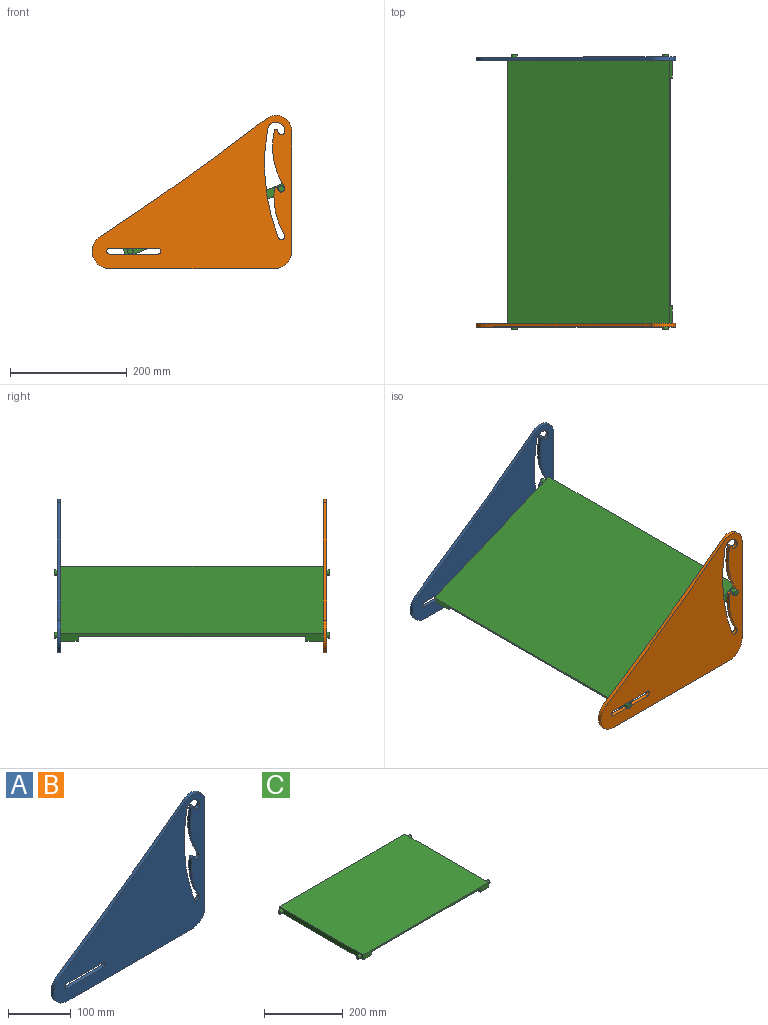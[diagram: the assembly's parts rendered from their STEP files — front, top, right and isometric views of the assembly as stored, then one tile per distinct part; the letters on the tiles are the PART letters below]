
ASSEMBLY  parts=3 mates=1
PART A: 21 faces, bbox 341.7x6x262.6 mm
  f0: cylinder r=5mm len=10mm, axis (0,1,0), area 94.2mm2, adj f1,f18,f19,f20
  f1: plane 82.5x6mm, normal (0,0,1), area 495mm2, adj f0,f2,f19,f20
  f2: cylinder r=5mm len=10mm, axis (0,1,0), area 94.2mm2, adj f1,f18,f19,f20
  f3: plane 281.72x6mm, normal (0,0,-1), area 1690.3mm2, adj f4,f16,f19,f20
  f4: cylinder r=30mm len=30mm, axis (0,1,0), area 282.7mm2, adj f3,f5,f19,f20
  f5: plane 205.78x6mm, normal (1,0,0), area 1234.7mm2, adj f4,f6,f19,f20
  f6: cylinder r=26.85mm len=42.37mm, axis (0,1,0), area 352.3mm2, adj f5,f7,f19,f20
  f7: cylinder r=4415.74mm len=285.72mm, axis (0,1,0), area 2101.9mm2, adj f6,f16,f19,f20
  f8: cylinder r=15mm len=29.78mm, axis (0,1,0), area 267.4mm2, adj f9,f17,f19,f20
  f9: cylinder r=6mm len=12mm, axis (0,1,0), area 113.1mm2, adj f8,f10,f19,f20
  f10: cylinder r=3mm len=6mm, axis (0,1,0), area 52.3mm2, adj f9,f11,f19,f20
  f11: cylinder r=125mm len=96.09mm, axis (0,1,0), area 601.5mm2, adj f10,f12,f19,f20
  f12: cylinder r=6mm len=12mm, axis (0,1,0), area 133.8mm2, adj f11,f13,f19,f20
  f13: cylinder r=3mm len=6mm, axis (0,1,0), area 54.5mm2, adj f12,f14,f19,f20
  f14: cylinder r=125mm len=78.66mm, axis (0,1,0), area 491.7mm2, adj f13,f15,f19,f20
  f15: cylinder r=6mm len=11.6mm, axis (0,1,0), area 119.4mm2, adj f14,f17,f19,f20
  f16: cylinder r=30mm len=55.14mm, axis (0,1,0), area 461.6mm2, adj f3,f7,f19,f20
  f17: cylinder r=350mm len=184.76mm, axis (0,1,0), area 1127.4mm2, adj f8,f15,f19,f20
  f18: plane 82.5x6mm, normal (0,0,-1), area 495mm2, adj f0,f2,f19,f20
  f19: plane 341.72x262.62mm, normal (0,-1,0), area 51054.7mm2, adj f0,f1,f2,f3,f4,f5,f6,f7
  f20: plane 341.72x262.62mm, normal (0,1,0), area 51054.7mm2, adj f0,f1,f2,f3,f4,f5,f6,f7
PART B: same geometry as A
PART C: 18 faces, bbox 470x300x15 mm
  f0: plane 390x300mm, normal (0,0,-1), area 117000mm2, adj f1,f3,f6,f8
  f1: plane 450x15mm, normal (0,-1,0), area 2850mm2, adj f0,f2,f4,f5,f6,f7,f8,f9
  f2: plane 300x15mm, normal (1,0,0), area 4342.9mm2, adj f1,f3,f5,f7,f10,f12
  f3: plane 450x15mm, normal (0,1,0), area 2850mm2, adj f0,f2,f4,f5,f6,f7,f8,f9
  f4: plane 300x15mm, normal (-1,0,0), area 4342.9mm2, adj f1,f3,f5,f9,f14,f16
  f5: plane 450x300mm, normal (0,0,1), area 135000mm2, adj f1,f2,f3,f4
  f6: plane 300x10mm, normal (-1,0,0), area 3000mm2, adj f0,f1,f3,f7
  f7: plane 300x30mm, normal (0,0,-1), area 9000mm2, adj f1,f2,f3,f6
  f8: plane 300x10mm, normal (1,0,0), area 3000mm2, adj f0,f1,f3,f9
  f9: plane 300x30mm, normal (0,0,-1), area 9000mm2, adj f1,f3,f4,f8
  f10: cylinder r=5mm len=10mm, axis (-1,0,0), area 314.2mm2, adj f2,f11
  f11: plane 10x10mm, normal (1,0,0), area 78.5mm2, adj f10
  f12: cylinder r=5mm len=10mm, axis (-1,0,0), area 314.2mm2, adj f2,f13
  f13: plane 10x10mm, normal (1,0,0), area 78.5mm2, adj f12
  f14: cylinder r=5mm len=10mm, axis (1,0,0), area 314.2mm2, adj f4,f15
  f15: plane 10x10mm, normal (-1,0,0), area 78.5mm2, adj f14
  f16: cylinder r=5mm len=10mm, axis (1,0,0), area 314.2mm2, adj f4,f17
  f17: plane 10x10mm, normal (-1,0,0), area 78.5mm2, adj f16
PLACE A t=(-97.29,100.37,-10.99)mm fixed
PLACE B t=(-97.29,-355.63,-10.99)mm fixed
PLACE C rot(axis=(-0.19,-0.19,0.96),92.2deg) t=(66.29,-130.57,44.87)mm
MATE cylindrical C.f14 <-> B.f12  axis (0,1,0) through (196.59,-365.57,96.13)mm
